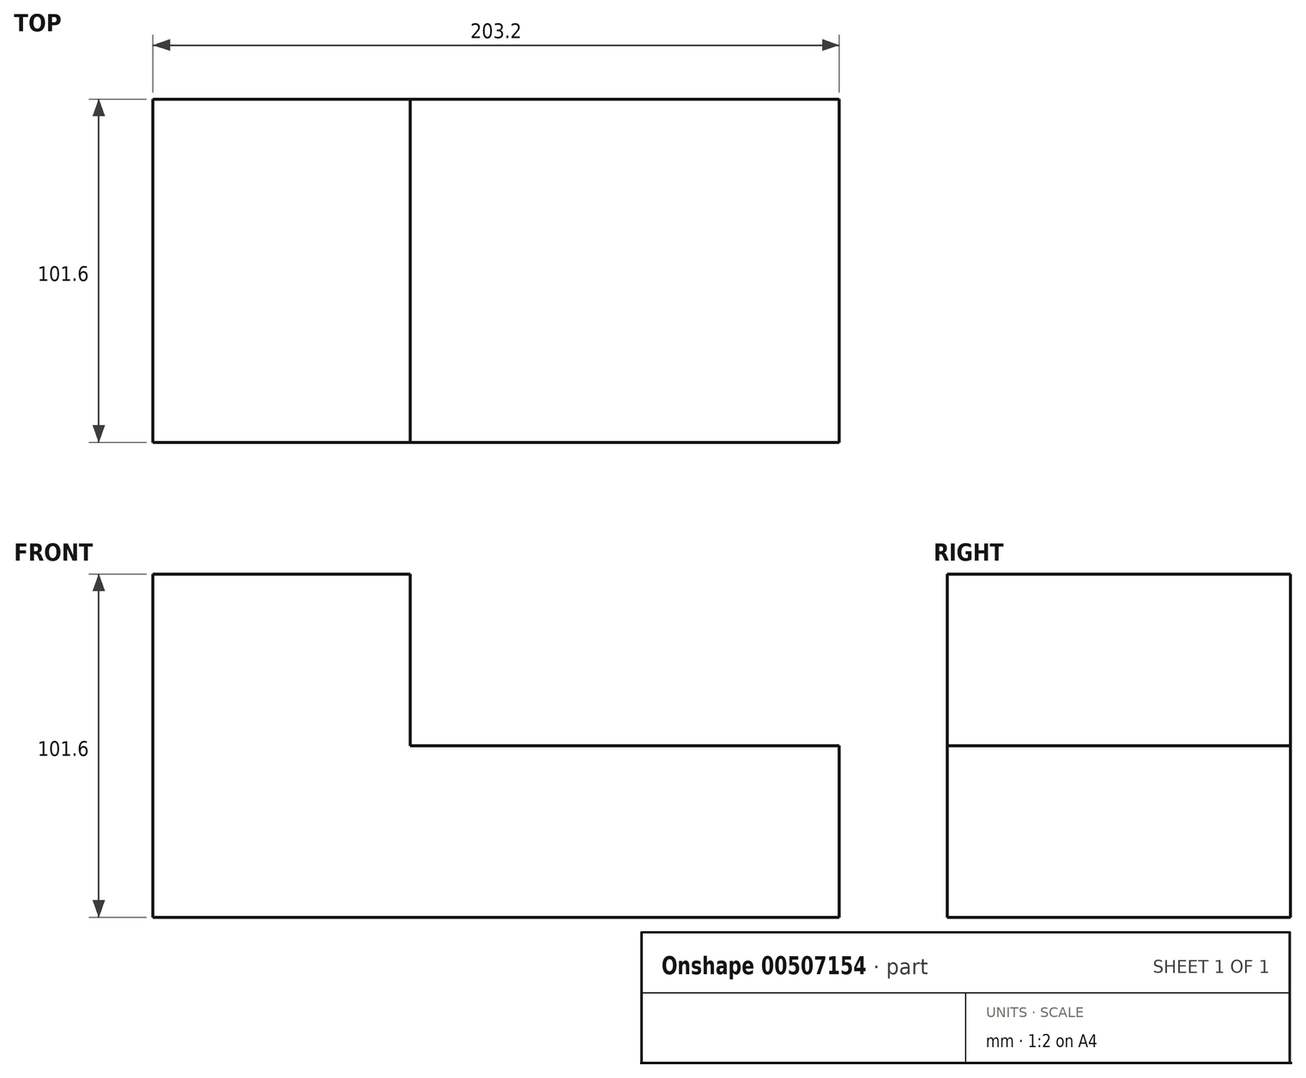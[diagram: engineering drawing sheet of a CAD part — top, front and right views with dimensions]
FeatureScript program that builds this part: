
annotation { "Feature Type Name" : "Feature", "Feature Type Description" : "" }
export const myFeature = defineFeature(function(context is Context, id is Id, definition is map)
    precondition{}
    {
        {
            var Q0;
            Q0=qCreatedBy(makeId("Front.planeOp"),FACE);
            var sketch = newSketch(context, id + "F0", { "sketchPlane" : qUnion([Q0])});
            skLineSegment(sketch, "E0", {"start": v(-86.81, 34.93) * mm, "end": v(-86.81, -66.67) * mm});
            skLineSegment(sketch, "E1", {"start": v(-86.81, -66.67) * mm, "end": v(116.39, -66.67) * mm});
            skLineSegment(sketch, "E2", {"start": v(116.39, -66.67) * mm, "end": v(116.39, -15.87) * mm});
            skLineSegment(sketch, "E3", {"start": v(116.39, -15.87) * mm, "end": v(-10.61, -15.87) * mm});
            skLineSegment(sketch, "E4", {"start": v(-10.61, -15.87) * mm, "end": v(-10.61, 34.93) * mm});
            skLineSegment(sketch, "E5", {"start": v(-10.61, 34.93) * mm, "end": v(-86.81, 34.93) * mm});
            skSolve(sketch);
        }
        {
            var Q0;
            Q0 = qSketchRegion(id + "F0", true);
            extrude(context, id + "F1", {"entities" : qUnion([Q0]), "depth" : 101.6 * mm});
        }
    });
